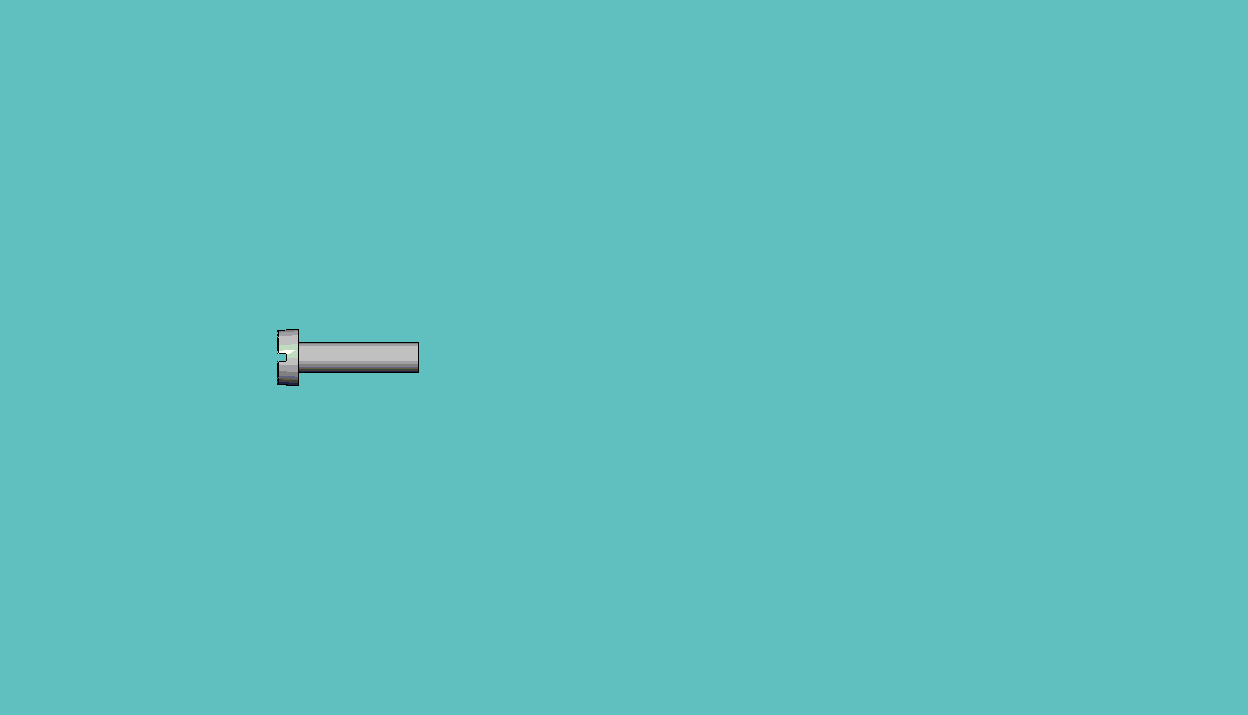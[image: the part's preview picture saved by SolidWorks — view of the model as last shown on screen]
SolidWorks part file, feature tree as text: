
SOLIDWORKS PART (.sldprt)
format: sldprt  version: not decoded by parser v0  size: 172,032 bytes
history: native  units: mm
features: plane x3, sketch x3, fillet x2, material x1, revolve x1, thread x1, cut_extrude x1, cut_revolve x1, pattern_linear x1 (+8 scaffold rows collapsed)
feature tree (22):
  scaffold x8  (default folders/planes/origin — collapsed)
  material  "Matériau <non spécifié>"
  plane  "Plane1"
  plane  "Plane2"
  plane  "Plane3"
  sketch  "BodySke"  dims[c1.Head_fillet_rad=3.6322mm c1.D1=~7.099516mm c1.Head_ang=85.0deg c1.Oval_ht=2.3876mm c1.Head_ht=6.1976mm c1.Diameter=9.525mm c1.Length=76.2mm c1.Head_dia=20.0152mm c2.Head_dia=15.3924mm c2.Head_ht=8.509mm c2.Length=8.0mm c2.Head_side_ht=6.1722mm c3.Head_ht=1.4mm c3.Head_dia=18.4912mm c3.Advance=0.4mm c3.Thread_nom=8.0mm c3.Thread_lim=36.5125mm c4.Head_dia=3.8mm c4.D2=152.4mm c4.Head_side_angle=5.0deg c4.Diameter=2.0mm]
  revolve  "Base-Revolve"  [1 undecoded]
  thread  "ThreadCosmetic"  Diameter=7.2mm Thread_length=7.2mm Thread_minor=1.548mm  [1 undecoded]
  fillet  "Fillet1"  Radius=0.1mm Head_dia=3.8mm Diameter=2mm
  fillet  "Fillet2"  Radius=0.1mm
  sketch  "Sketch2"  dims[D1=3.8mm Slot_width=0.5mm D2=1.9mm D3=0.25mm]
  cut_extrude  "Slot"  Depth=0.6mm Slot_depth=0.6mm
  sketch  "ThdSchSke"  dims[c1.Thread_minor=~1.03886mm c1.Diameter=~1.413535mm c1.Start=~0.988134mm c1.D4=~4.446753mm c1.Vee=60.0deg c2.Thread_minor=~1.03886mm c2.Start=~2.540025mm c2.D1=~0.108159mm c2.D2=~0.108159mm c3.D1=~0.216319mm c3.SideAngle=55.0deg c3.D2=~0.216319mm c3.VeeAngle=70.0deg c3.Thread_minor=1.548mm c3.Overcut=2.5mm c3.Diameter=2.0mm c3.D6=~8.326268mm c4.D1=~8.326268mm c5.D1=90.0deg c5.Start=11.1125mm c6.Start=~44.450025mm c7.Start=2.2mm]
  cut_revolve  "ThreadSchematic"  Angle=360deg
  pattern_linear  "ThdSchPat"  Count1=19 Count2=1 Spacing1=0.4mm Spacing2=50mm Num_threads=19 Advance=0.4mm ConfigurationName=0mm CopiedFlag=1 PartNumberID=0mm
decode coverage: 9 of 10 modeling features carry decoded parameters
note: ~ marks probable driven/reference dimensions
note: 2 parameter values undecoded
note: suppression state not decoded; provenance and decode notes live in map.json
